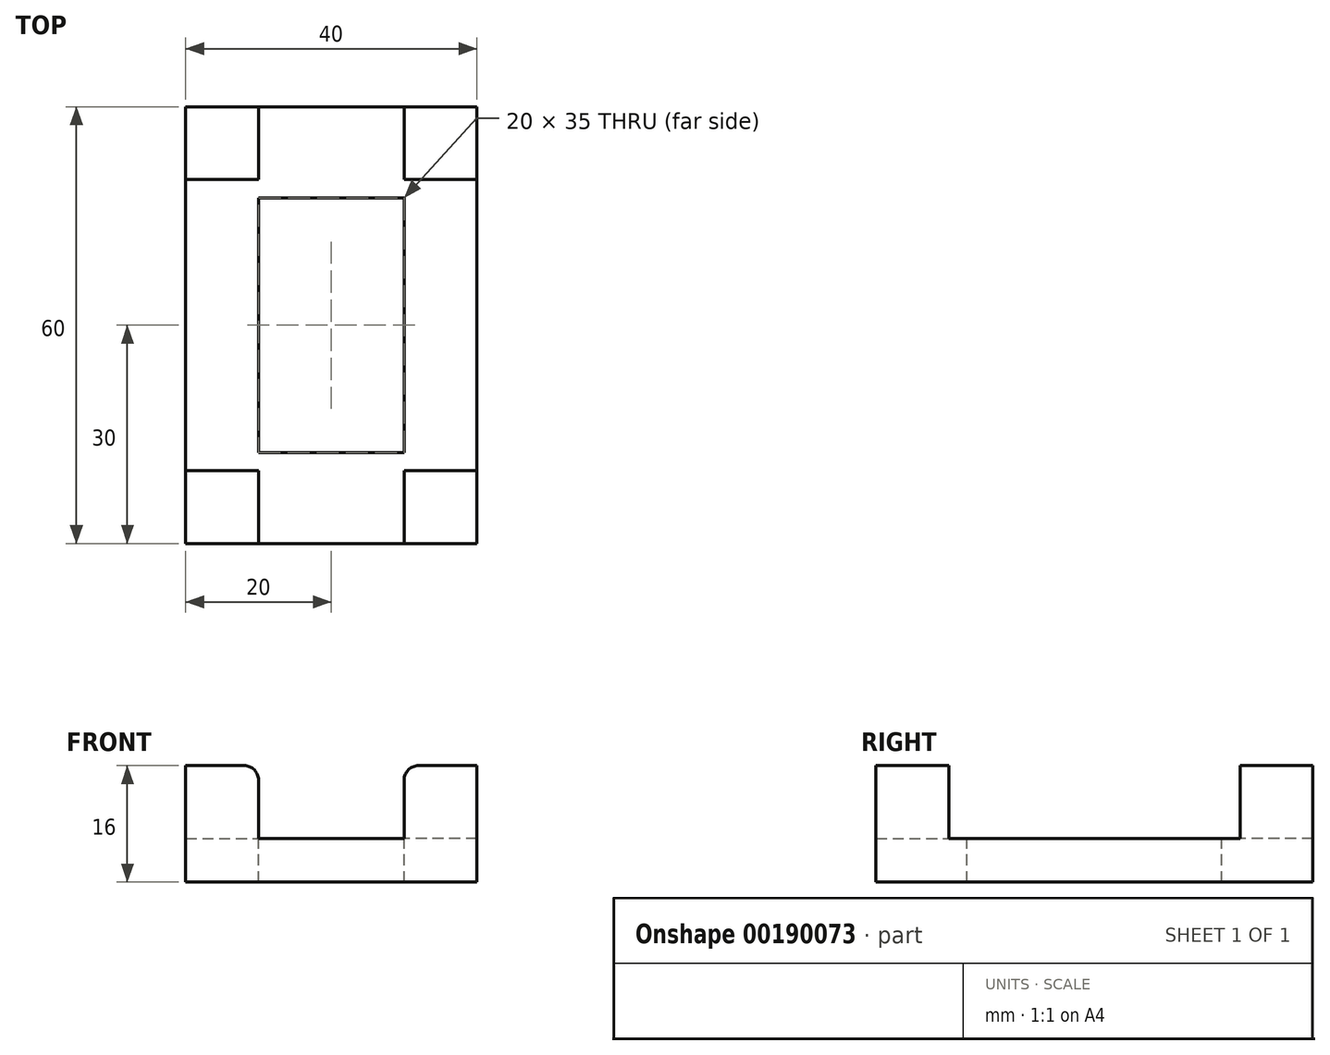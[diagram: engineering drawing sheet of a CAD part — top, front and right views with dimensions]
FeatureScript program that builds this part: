
annotation { "Feature Type Name" : "Feature", "Feature Type Description" : "" }
export const myFeature = defineFeature(function(context is Context, id is Id, definition is map)
    precondition{}
    {
        {
            var Q0;
            Q0=qCreatedBy(makeId("Top.planeOp"),FACE);
            var sketch = newSketch(context, id + "F0", { "sketchPlane" : qUnion([Q0])});
            skLineSegment(sketch, "E0.bottom", {"start": v(20, -30) * mm, "end": v(-20, -30) * mm});
            skLineSegment(sketch, "E0.top", {"start": v(20, 30) * mm, "end": v(-20, 30) * mm});
            skLineSegment(sketch, "E0.left", {"start": v(20, -30) * mm, "end": v(20, 30) * mm});
            skLineSegment(sketch, "E0.right", {"start": v(-20, -30) * mm, "end": v(-20, 30) * mm});
            skPoint(sketch, "E0.middle", {"position": v(0, 0) * mm});
            skSolve(sketch);
        }
        {
            var Q0;
            Q0=qSketchRegion(id+"F0",true);
            extrude(context, id + "F1", {"entities" : qUnion([Q0]), "oppositeDirection" : true, "depth" : 6 * mm});
        }
        {
            var Q0;
            Q0=makeQuery(id+"F1.opExtrude","CAP_FACE",FACE,{"disambiguationData":[OSD([sQuery(id+"F0.wireOp",EDGE,"E0.bottom"),sQuery(id+"F0.wireOp",EDGE,"E0.top"),sQuery(id+"F0.wireOp",EDGE,"E0.left"),sQuery(id+"F0.wireOp",EDGE,"E0.right")])],"isStart":true});
            var sketch = newSketch(context, id + "F2", { "sketchPlane" : qUnion([Q0])});
            skLineSegment(sketch, "E1.bottom", {"start": v(-20, 30) * mm, "end": v(-10, 30) * mm});
            skLineSegment(sketch, "E1.top", {"start": v(-20, 20) * mm, "end": v(-10, 20) * mm});
            skLineSegment(sketch, "E1.left", {"start": v(-20, 30) * mm, "end": v(-20, 20) * mm});
            skLineSegment(sketch, "E1.right", {"start": v(-10, 30) * mm, "end": v(-10, 20) * mm});
            skLineSegment(sketch, "E2.bottom", {"start": v(20, 30) * mm, "end": v(10, 30) * mm});
            skLineSegment(sketch, "E2.top", {"start": v(20, 20) * mm, "end": v(10, 20) * mm});
            skLineSegment(sketch, "E2.left", {"start": v(20, 30) * mm, "end": v(20, 20) * mm});
            skLineSegment(sketch, "E2.right", {"start": v(10, 30) * mm, "end": v(10, 20) * mm});
            skLineSegment(sketch, "E3.bottom", {"start": v(-20, -30) * mm, "end": v(-10, -30) * mm});
            skLineSegment(sketch, "E3.top", {"start": v(-20, -20) * mm, "end": v(-10, -20) * mm});
            skLineSegment(sketch, "E3.left", {"start": v(-20, -30) * mm, "end": v(-20, -20) * mm});
            skLineSegment(sketch, "E3.right", {"start": v(-10, -30) * mm, "end": v(-10, -20) * mm});
            skLineSegment(sketch, "E4.bottom", {"start": v(20, -30) * mm, "end": v(10, -30) * mm});
            skLineSegment(sketch, "E4.top", {"start": v(20, -20) * mm, "end": v(10, -20) * mm});
            skLineSegment(sketch, "E4.left", {"start": v(20, -30) * mm, "end": v(20, -20) * mm});
            skLineSegment(sketch, "E4.right", {"start": v(10, -30) * mm, "end": v(10, -20) * mm});
            skSolve(sketch);
        }
        {
            var Q0;
            Q0=makeQuery(id+"F2.imprint","IMPRINT",FACE,{"disambiguationData":[TD([[makeQuery(id+"F2.imprint","IMPRINT",EDGE,{"derivedFrom":sQuery(id+"F2.wireOp",EDGE,"E1.bottom")}),1.0]])]});
            var Q1;
            Q1=makeQuery(id+"F2.imprint","IMPRINT",FACE,{"disambiguationData":[TD([[makeQuery(id+"F2.imprint","IMPRINT",EDGE,{"derivedFrom":sQuery(id+"F2.wireOp",EDGE,"E2.bottom")}),1.0]])]});
            var Q2;
            Q2=makeQuery(id+"F2.imprint","IMPRINT",FACE,{"disambiguationData":[TD([[makeQuery(id+"F2.imprint","IMPRINT",EDGE,{"derivedFrom":sQuery(id+"F2.wireOp",EDGE,"E4.bottom")}),-1.0]])]});
            var Q3;
            Q3=makeQuery(id+"F2.imprint","IMPRINT",FACE,{"disambiguationData":[TD([[makeQuery(id+"F2.imprint","IMPRINT",EDGE,{"derivedFrom":sQuery(id+"F2.wireOp",EDGE,"E3.bottom")}),-1.0]])]});
            extrude(context, id + "F3", {"entities" : qUnion([Q0, Q1, Q2, Q3]), "operationType" : NewBodyOperationType.ADD, "depth" : 10 * mm});
        }
        {
            var Q0;
            Q0=makeQuery(id+"F3.opExtrude","CAP_FACE",FACE,{"disambiguationData":[OSD([sQuery(id+"F2.wireOp",EDGE,"E1.bottom"),sQuery(id+"F2.wireOp",EDGE,"E1.top"),sQuery(id+"F2.wireOp",EDGE,"E1.left"),sQuery(id+"F2.wireOp",EDGE,"E1.right")])],"isStart":false});
            var sketch = newSketch(context, id + "F4", { "sketchPlane" : qUnion([Q0])});
            skLineSegment(sketch, "E5.bottom", {"start": v(-20, 30) * mm, "end": v(-15, 30) * mm, "construction": true});
            skLineSegment(sketch, "E5.top", {"start": v(-20, 25) * mm, "end": v(-15, 25) * mm, "construction": true});
            skLineSegment(sketch, "E5.left", {"start": v(-20, 30) * mm, "end": v(-20, 25) * mm, "construction": true});
            skLineSegment(sketch, "E5.right", {"start": v(-15, 30) * mm, "end": v(-15, 25) * mm, "construction": true});
            skSolve(sketch);
        }
        {
            var Q0;
            Q0=makeQuery(id+"F3.opExtrude","CAP_FACE",FACE,{"disambiguationData":[OSD([sQuery(id+"F2.wireOp",EDGE,"E2.bottom"),sQuery(id+"F2.wireOp",EDGE,"E2.top"),sQuery(id+"F2.wireOp",EDGE,"E2.left"),sQuery(id+"F2.wireOp",EDGE,"E2.right")])],"isStart":false});
            var sketch = newSketch(context, id + "F5", { "sketchPlane" : qUnion([Q0])});
            skPoint(sketch, "E6.oppositeSnap0", {"position": v(20, 25) * mm});
            skPoint(sketch, "E6.oppositeSnap1", {"position": v(15, 20) * mm});
            skLineSegment(sketch, "E6.bottom", {"start": v(20, 30) * mm, "end": v(15, 30) * mm, "construction": true});
            skLineSegment(sketch, "E6.top", {"start": v(20, 25) * mm, "end": v(15, 25) * mm, "construction": true});
            skLineSegment(sketch, "E6.left", {"start": v(20, 30) * mm, "end": v(20, 25) * mm, "construction": true});
            skLineSegment(sketch, "E6.right", {"start": v(15, 30) * mm, "end": v(15, 25) * mm, "construction": true});
            skSolve(sketch);
        }
        {
            var Q0;
            Q0=makeQuery(id+"F3.opExtrude","CAP_FACE",FACE,{"disambiguationData":[OSD([sQuery(id+"F2.wireOp",EDGE,"E3.bottom"),sQuery(id+"F2.wireOp",EDGE,"E3.top"),sQuery(id+"F2.wireOp",EDGE,"E3.left"),sQuery(id+"F2.wireOp",EDGE,"E3.right")])],"isStart":false});
            var sketch = newSketch(context, id + "F6", { "sketchPlane" : qUnion([Q0])});
            skPoint(sketch, "E7.oppositeSnap0", {"position": v(-20, -25) * mm});
            skLineSegment(sketch, "E7.bottom", {"start": v(-10, -20) * mm, "end": v(-15, -20) * mm, "construction": true});
            skLineSegment(sketch, "E7.top", {"start": v(-10, -25) * mm, "end": v(-15, -25) * mm, "construction": true});
            skLineSegment(sketch, "E7.left", {"start": v(-10, -20) * mm, "end": v(-10, -25) * mm, "construction": true});
            skLineSegment(sketch, "E7.right", {"start": v(-15, -20) * mm, "end": v(-15, -25) * mm, "construction": true});
            skSolve(sketch);
        }
        {
            var Q0;
            Q0=makeQuery(id+"F3.opExtrude","CAP_FACE",FACE,{"disambiguationData":[OSD([sQuery(id+"F2.wireOp",EDGE,"E4.bottom"),sQuery(id+"F2.wireOp",EDGE,"E4.top"),sQuery(id+"F2.wireOp",EDGE,"E4.left"),sQuery(id+"F2.wireOp",EDGE,"E4.right")])],"isStart":false});
            var sketch = newSketch(context, id + "F7", { "sketchPlane" : qUnion([Q0])});
            skLineSegment(sketch, "E8.bottom", {"start": v(10, -20) * mm, "end": v(15, -20) * mm, "construction": true});
            skLineSegment(sketch, "E8.top", {"start": v(10, -25) * mm, "end": v(15, -25) * mm, "construction": true});
            skLineSegment(sketch, "E8.left", {"start": v(10, -20) * mm, "end": v(10, -25) * mm, "construction": true});
            skLineSegment(sketch, "E8.right", {"start": v(15, -20) * mm, "end": v(15, -25) * mm, "construction": true});
            skSolve(sketch);
        }
        {
            var Q0;
            Q0=makeQuery(id+"F4.imprint","IMPRINT",FACE,{"disambiguationData":[TD([[makeQuery(id+"F4.imprint","IMPRINT",EDGE,{"derivedFrom":makeQuery(id+"F3.opExtrude","CAP_EDGE",EDGE,{"disambiguationData":[OSD([sQuery(id+"F2.wireOp",EDGE,"E1.bottom")])],"isStart":false})}),1.0]])]});
            var sketch = newSketch(context, id + "F8", { "sketchPlane" : qUnion([Q0])});
            skCircle(sketch, "E9", {"center": v(-15.21, 25.2) * mm, "radius": 2.5 * mm});
            skSolve(sketch);
        }
        {
            var Q0;
            Q0=makeQuery(id+"F5.imprint","IMPRINT",FACE,{"disambiguationData":[TD([[makeQuery(id+"F5.imprint","IMPRINT",EDGE,{"derivedFrom":makeQuery(id+"F3.opExtrude","CAP_EDGE",EDGE,{"disambiguationData":[OSD([sQuery(id+"F2.wireOp",EDGE,"E2.bottom")])],"isStart":false})}),1.0]])]});
            var sketch = newSketch(context, id + "F9", { "sketchPlane" : qUnion([Q0])});
            skCircle(sketch, "E10", {"center": v(15.02, 24.94) * mm, "radius": 2.48 * mm});
            skSolve(sketch);
        }
        {
            var Q0;
            Q0=makeQuery(id+"F6.imprint","IMPRINT",FACE,{"disambiguationData":[TD([[makeQuery(id+"F6.imprint","IMPRINT",EDGE,{"derivedFrom":makeQuery(id+"F3.opExtrude","CAP_EDGE",EDGE,{"disambiguationData":[OSD([sQuery(id+"F2.wireOp",EDGE,"E3.bottom")])],"isStart":false})}),-1.0]])]});
            var sketch = newSketch(context, id + "F10", { "sketchPlane" : qUnion([Q0])});
            skCircle(sketch, "E11", {"center": v(-14.84, -25.18) * mm, "radius": 2.5 * mm});
            skSolve(sketch);
        }
        {
            var Q0;
            Q0=makeQuery(id+"F7.imprint","IMPRINT",FACE,{"disambiguationData":[TD([[makeQuery(id+"F7.imprint","IMPRINT",EDGE,{"derivedFrom":makeQuery(id+"F3.opExtrude","CAP_EDGE",EDGE,{"disambiguationData":[OSD([sQuery(id+"F2.wireOp",EDGE,"E4.bottom")])],"isStart":false})}),-1.0]])]});
            var sketch = newSketch(context, id + "F11", { "sketchPlane" : qUnion([Q0])});
            skCircle(sketch, "E12", {"center": v(14.9, -25.43) * mm, "radius": 2.5 * mm});
            skSolve(sketch);
        }
        {
            var Q0;
            Q0=sQuery(id+"F8.wireOp",EDGE,"E9");
            var Q1;
            Q1=sQuery(id+"F9.wireOp",EDGE,"E10");
            var Q2;
            Q2=sQuery(id+"F11.wireOp",EDGE,"E12");
            var Q3;
            Q3=sQuery(id+"F10.wireOp",EDGE,"E11");
            extrude(context, id + "F12", {"bodyType" : ToolBodyType.SURFACE, "surfaceEntities" : qUnion([Q0, Q1, Q2, Q3]), "depth" : 4 * mm});
        }
        {
            var Q0;
            Q0=makeQuery(id+"F3.opExtrude","CAP_EDGE",EDGE,{"disambiguationData":[OSD([sQuery(id+"F2.wireOp",EDGE,"E1.right")])],"isStart":false});
            var Q1;
            Q1=makeQuery(id+"F3.opExtrude","CAP_EDGE",EDGE,{"disambiguationData":[OSD([sQuery(id+"F2.wireOp",EDGE,"E3.right")])],"isStart":false});
            var Q2;
            Q2=makeQuery(id+"F3.opExtrude","CAP_EDGE",EDGE,{"disambiguationData":[OSD([sQuery(id+"F2.wireOp",EDGE,"E3.right")])],"isStart":true});
            var Q3;
            Q3=makeQuery(id+"F3.opExtrude","CAP_EDGE",EDGE,{"disambiguationData":[OSD([sQuery(id+"F2.wireOp",EDGE,"E1.right")])],"isStart":true});
            var Q4;
            Q4=makeQuery(id+"F3.opExtrude","CAP_EDGE",EDGE,{"disambiguationData":[OSD([sQuery(id+"F2.wireOp",EDGE,"E4.right")])],"isStart":false});
            var Q5;
            Q5=makeQuery(id+"F3.opExtrude","CAP_EDGE",EDGE,{"disambiguationData":[OSD([sQuery(id+"F2.wireOp",EDGE,"E2.right")])],"isStart":false});
            var Q6;
            Q6=makeQuery(id+"F3.opExtrude","CAP_EDGE",EDGE,{"disambiguationData":[OSD([sQuery(id+"F2.wireOp",EDGE,"E4.right")])],"isStart":true});
            var Q7;
            Q7=makeQuery(id+"F3.opExtrude","CAP_EDGE",EDGE,{"disambiguationData":[OSD([sQuery(id+"F2.wireOp",EDGE,"E2.right")])],"isStart":true});
            fillet(context, id + "F13", {"entities" : qUnion([Q0, Q1, Q2, Q3, Q4, Q5, Q6, Q7]), "radius" : 2 * mm, "tangentPropagation" : true, "allowEdgeOverflow" : false});
        }
        {
            var Q0;
            Q0=makeQuery(id+"F1.opExtrude","CAP_FACE",FACE,{"disambiguationData":[OSD([sQuery(id+"F0.wireOp",EDGE,"E0.bottom"),sQuery(id+"F0.wireOp",EDGE,"E0.top"),sQuery(id+"F0.wireOp",EDGE,"E0.left"),sQuery(id+"F0.wireOp",EDGE,"E0.right")])],"isStart":true});
            var sketch = newSketch(context, id + "F14", { "sketchPlane" : qUnion([Q0])});
            skLineSegment(sketch, "E13.bottom", {"start": v(10, -17.5) * mm, "end": v(-10, -17.5) * mm});
            skLineSegment(sketch, "E13.top", {"start": v(10, 17.5) * mm, "end": v(-10, 17.5) * mm});
            skLineSegment(sketch, "E13.left", {"start": v(10, -17.5) * mm, "end": v(10, 17.5) * mm});
            skLineSegment(sketch, "E13.right", {"start": v(-10, -17.5) * mm, "end": v(-10, 17.5) * mm});
            skPoint(sketch, "E13.middle", {"position": v(0, 0) * mm});
            skSolve(sketch);
        }
        {
            var Q0;
            Q0=qSketchRegion(id+"F14",true);
            extrude(context, id + "F15", {"entities" : qUnion([Q0]), "operationType" : NewBodyOperationType.REMOVE, "oppositeDirection" : true, "depth" : 25 * mm});
        }
    });
